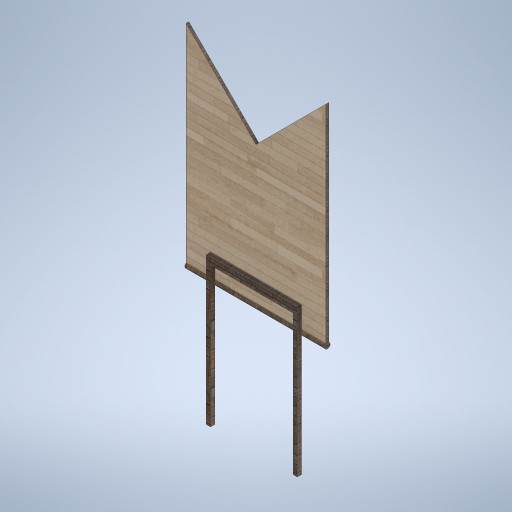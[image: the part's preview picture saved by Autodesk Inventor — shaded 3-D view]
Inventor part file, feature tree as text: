
AUTODESK INVENTOR PART (.ipt)
format: ipt  version: 2024.2 (Build 282272000, 272)  size: 372,224 bytes
history: native  units: mm
features: extrude x5, sketch x4, other x1
ambient origin geometry x8: Origin, YZ Plane, XZ Plane, XY Plane, X Axis, Y Axis, Z Axis, Center Point
bodies: Body1 (feature_tree)
feature tree (10):
  other  "實體1"
  extrude  "擠出1"  Depth=1500.0mm
  extrude  "擠出2"  Depth=1000.0mm
  extrude  "擠出3"  Depth=20.0mm TaperAngle=0.0deg
  sketch  "草圖4"
  extrude  "擠出4"  Depth=40.0mm
  extrude  "擠出5"  Depth=1000.0mm TaperAngle=0.0deg
  sketch  "草圖1"
  sketch  "草圖2"
  sketch  "草圖3"
